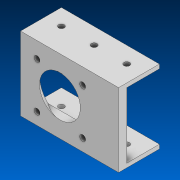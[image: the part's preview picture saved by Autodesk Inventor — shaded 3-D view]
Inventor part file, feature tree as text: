
AUTODESK INVENTOR PART (.ipt)
format: ipt  version: 2022.2 (Build 262287000, 287)  size: 168,960 bytes
history: native  units: in
note: dims shown in document units (in); Inventor stores cm internally (conversion verified against a paired STEP export)
features: sketch x5, extrude x3, hole x2, chamfer x1
ambient origin geometry x8: Origin, YZ Plane, XZ Plane, XY Plane, X Axis, Y Axis, Z Axis, Center Point
bodies: Solid1 (feature_tree)
feature tree (11):
  extrude  "Extrusion1"  Depth=2.0in
  chamfer  "Chamfer1"  Distance=1.0in
  extrude  "Extrusion2"  Depth=0.75in TaperAngle=0.0deg
  hole  "Hole1"  [1 undecoded]
  extrude  "Extrusion3"  Depth=0.125in
  hole  "Hole2"  [1 undecoded]
  sketch  "Sketch1"  dims[d0=1.25in d1=2.0in]
  sketch  "Sketch2"  dims[d3=0.2965in]
  sketch  "Sketch3"  dims[d6=1.5in]
  sketch  "Sketch4"  dims[d7=1.5in]
  sketch  "Sketch5"  dims[d8=1.0in d9=1.0in d10=0.25in d11=0.0in d12=0.25in d13=0.25in d14=45.0deg d15=0.125in d16=1.0in d17=0.25in d18=0.0in d19=0.5in d20=1.0in d21=1.0in d22=0.5in d23=0.175in d24=0.75in d25=0.375in d26=0.25in d27=0.5635in d28=1.0in d29=0.8108in d30=1.0in d31=0.0in d32=0.0625in d34=1.975in d35=0.18in d36=0.75in d37=0.375in d38=0.25in d39=0.5635in d40=1.0in d41=0.8108in]
note: 2 required parameter values undecoded (feature->parameter linkage not recoverable at this tier; creation-order binding heuristic only, values carry confidence <= 0.55)
